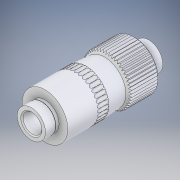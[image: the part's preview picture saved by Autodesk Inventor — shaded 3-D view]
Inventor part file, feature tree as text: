
AUTODESK INVENTOR PART (.ipt)
format: ipt  version: 2017 (Build 210142000, 142)  size: 670,208 bytes
history: native  units: in
note: dims shown in document units (in); Inventor stores cm internally (conversion verified against a paired STEP export)
features: sketch x3, revolve x2, pattern_circular x2, plane x2, extrude x1, chamfer x1
ambient origin geometry x8: Origin, YZ Plane, XZ Plane, XY Plane, X Axis, Y Axis, Z Axis, Center Point
bodies: Solid1 (feature_tree)
feature tree (11):
  revolve  "Revolution1"  [1 undecoded]
  extrude  "Extrusion1"  Depth=0.002in
  pattern_circular  "Circular Pattern1"  [2 undecoded]
  plane  "Work Plane1"
  revolve  "Revolution2"  Angle=135.0deg
  pattern_circular  "Circular Pattern2"  [2 undecoded]
  chamfer  "Chamfer1"  Distance=0.315in
  plane  "Work Plane2"
  sketch  "Sketch1"  dims[d0=0.1299in d1=0.1949in]
  sketch  "Sketch2"  dims[d3=0.002in d4=0.002in]
  sketch  "Sketch3"  dims[d5=0.0709in d6=0.3386in d7=135.0deg d8=0.0945in d9=0.315in d10=0.1772in d11=135.0deg d12=0.2953in d13=0.002in d14=0.002in d16=0.811in d17=0.0709in d19=0.315in d20=0.0945in d21=90.0deg d22=0.2835in d23=0.3386in d24=0.0247in d26=0.1575in d27=0.2362in d28=0.0in d29=19.685in d30=360.0deg d32=-0.2441in d33=0.2264in d35=0.1614in d36=0.315in d37=0.0275in d38=90.0deg d40=14.1732in d41=360.0deg d46=0.0079in d47=0.0787in d48=45.0deg d49=0.1949in d50=-0.1949in]
note: 5 required parameter values undecoded (feature->parameter linkage not recoverable at this tier; creation-order binding heuristic only, values carry confidence <= 0.55)